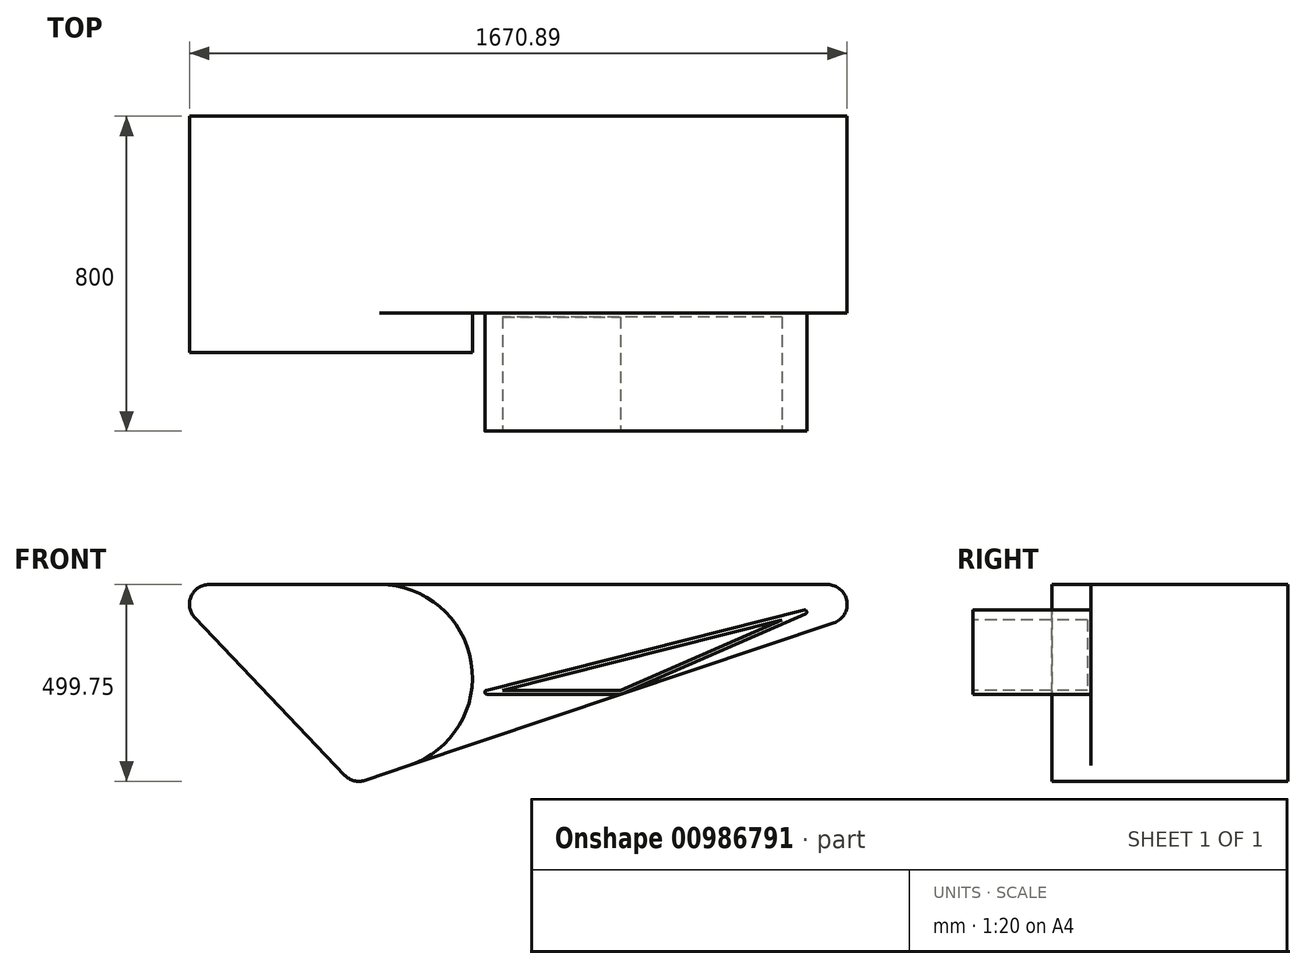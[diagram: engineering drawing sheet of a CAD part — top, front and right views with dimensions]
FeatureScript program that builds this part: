
annotation { "Feature Type Name" : "Feature", "Feature Type Description" : "" }
export const myFeature = defineFeature(function(context is Context, id is Id, definition is map)
    precondition{}
    {
        {
            var Q0;
            Q0=qCreatedBy(makeId("Front.planeOp"),FACE);
            var sketch = newSketch(context, id + "F0", { "sketchPlane" : qUnion([Q0])});
            skLineSegment(sketch, "E0", {"start": v(-637.35, 0) * mm, "end": v(-155, -507.28) * mm});
            skLineSegment(sketch, "E1", {"start": v(1356.12, 0) * mm, "end": v(-155, -507.28) * mm});
            skLineSegment(sketch, "E2", {"start": v(-637.35, 0) * mm, "end": v(1356.12, 0) * mm});
            skSolve(sketch);
        }
        {
            var Q0;
            Q0=makeQuery(id+"F0.imprint","IMPRINT",FACE,{"disambiguationData":[TD([[makeQuery(id+"F0.imprint","IMPRINT",EDGE,{"derivedFrom":sQuery(id+"F0.wireOp",EDGE,"E0")}),1.0]])]});
            extrude(context, id + "F1", {"entities" : qUnion([Q0]), "depth" : 600 * mm, "offsetDistance" : 25 * mm});
        }
        {
            var Q0;
            Q0=makeQuery(id+"F1.opExtrude","SWEPT_EDGE",EDGE,{"disambiguationData":[OSD([sQuery(id+"F0.wireOp",EDGE,"E0"),sQuery(id+"F0.wireOp",EDGE,"E1")])]});
            var Q1;
            Q1=makeQuery(id+"F1.opExtrude","SWEPT_EDGE",EDGE,{"disambiguationData":[OSD([sQuery(id+"F0.wireOp",EDGE,"E1"),sQuery(id+"F0.wireOp",EDGE,"E2")])]});
            var Q2;
            Q2=makeQuery(id+"F1.opExtrude","SWEPT_EDGE",EDGE,{"disambiguationData":[OSD([sQuery(id+"F0.wireOp",EDGE,"E0"),sQuery(id+"F0.wireOp",EDGE,"E2")])]});
            fillet(context, id + "F2", {"entities" : qUnion([Q0, Q1, Q2]), "tangentPropagation" : true, "radius" : 50 * mm, "defaultsChanged" : false, "vertexSettings" : [], "allowEdgeOverflow" : false});
        }
        {
            var Q0;
            Q0=makeQuery(id+"F1.opExtrude","CAP_FACE",FACE,{"disambiguationData":[OSD([sQuery(id+"F0.wireOp",EDGE,"E0"),sQuery(id+"F0.wireOp",EDGE,"E1"),sQuery(id+"F0.wireOp",EDGE,"E2")])],"isStart":false});
            var sketch = newSketch(context, id + "F3", { "sketchPlane" : qUnion([Q0])});
            skCircle(sketch, "E3", {"center": v(-87.61, -235.86) * mm, "radius": 235.86 * mm});
            skPoint(sketch, "E3.first.point", {"position": v(-12.55, -459.46) * mm});
            skPoint(sketch, "E3.second.point", {"position": v(-323.14, -248.41) * mm});
            skPoint(sketch, "E3.third.point", {"position": v(-87.61, 0) * mm});
            skSolve(sketch);
        }
        {
            var Q0;
            {var subQ0=sQuery(id+"F3.wireOp",EDGE,"E3");var subQ1=sQuery(id+"F0.wireOp",EDGE,"E2");var subQ2=makeQuery(id+"F1.opExtrude","CAP_EDGE",EDGE,{"disambiguationData":[OSD([subQ1])],"isStart":false});var subQ3=makeQuery(id+"F3.imprint","INTERSECT",VERTEX,{"derivedFrom":[subQ2,subQ0]});Q0=makeQuery(id+"F3.imprint","IMPRINT",FACE,{"disambiguationData":[TD([[makeQuery(id+"F3.imprint","IMPRINT",EDGE,{"disambiguationData":[TD([[subQ3,1.0]])],"derivedFrom":subQ0}),-1.0]])]});}
            extrude(context, id + "F4", {"entities" : qUnion([Q0]), "operationType" : NewBodyOperationType.REMOVE, "oppositeDirection" : true, "depth" : 100 * mm, "offsetDistance" : 25 * mm});
        }
        {
            var Q0;
            Q0=makeQuery(id+"F4.boolean.opBoolean","COPY",FACE,{"derivedFrom":makeQuery(id+"F4.opExtrude","CAP_FACE",FACE,{"disambiguationData":[OSD([sQuery(id+"F0.wireOp",EDGE,"E0"),sQuery(id+"F0.wireOp",EDGE,"E1"),sQuery(id+"F0.wireOp",EDGE,"E2"),sQuery(id+"F3.wireOp",EDGE,"E3")])],"isStart":false})});
            var sketch = newSketch(context, id + "F5", { "sketchPlane" : qUnion([Q0])});
            skLineSegment(sketch, "E4", {"start": v(1050.07, -50) * mm, "end": v(144.38, -278.43) * mm});
            skPoint(sketch, "E4.endSnap0", {"position": v(526.71, -278.43) * mm});
            skLineSegment(sketch, "E5", {"start": v(144.38, -278.43) * mm, "end": v(526.71, -278.43) * mm});
            skLineSegment(sketch, "E6", {"start": v(1050.07, -50) * mm, "end": v(526.71, -278.43) * mm});
            skSolve(sketch);
        }
        {
            var Q0;
            Q0=makeQuery(id+"F5.imprint","IMPRINT",FACE,{"disambiguationData":[TD([[makeQuery(id+"F5.imprint","IMPRINT",EDGE,{"derivedFrom":sQuery(id+"F5.wireOp",EDGE,"E4")}),1.0]])]});
            extrude(context, id + "F6", {"entities" : qUnion([Q0]), "depth" : 300 * mm, "offsetDistance" : 25 * mm});
        }
        {
            var Q0;
            Q0=makeQuery(id+"F6.opExtrude","SWEPT_EDGE",EDGE,{"disambiguationData":[OSD([sQuery(id+"F3.wireOp",EDGE,"E3"),sQuery(id+"F5.wireOp",EDGE,"E4"),sQuery(id+"F5.wireOp",EDGE,"E5")])]});
            var Q1;
            Q1=makeQuery(id+"F6.opExtrude","SWEPT_EDGE",EDGE,{"disambiguationData":[OSD([sQuery(id+"F5.wireOp",EDGE,"E4"),sQuery(id+"F5.wireOp",EDGE,"E6")])]});
            var Q2;
            Q2=makeQuery(id+"F6.opExtrude","SWEPT_EDGE",EDGE,{"disambiguationData":[OSD([sQuery(id+"F0.wireOp",EDGE,"E1"),sQuery(id+"F5.wireOp",EDGE,"E5"),sQuery(id+"F5.wireOp",EDGE,"E6")])]});
            fillet(context, id + "F7", {"entities" : qUnion([Q0, Q1, Q2]), "tangentPropagation" : true, "radius" : 5 * mm, "defaultsChanged" : false, "vertexSettings" : [], "allowEdgeOverflow" : false});
        }
        {
            var Q0;
            Q0=makeQuery(id+"F6.opExtrude","CAP_FACE",FACE,{"disambiguationData":[OSD([sQuery(id+"F5.wireOp",EDGE,"E4"),sQuery(id+"F5.wireOp",EDGE,"E5"),sQuery(id+"F5.wireOp",EDGE,"E6")])],"isStart":false});
            shell(context, id + "F8", {"entities" : qUnion([Q0]), "thickness" : 10 * mm});
        }
    });
